# Revit family: Bath-Freestanding-KOHLER-ARCHER-K-45594T_1
name_source: partatom
category: Plumbing Fixtures
revit_build: Autodesk Revit 2017 (Build: 20160225_1515(x64)
units: mm (PartAtom-declared; Revit-internal decimal feet)

## family parameters
Cut with Voids When Loaded = No
Host = Face
OmniClass Number = 23.31.15.00
OmniClass Title = Bathtubs
Part Type = Normal
Room Calculation Point = No
Round Connector Dimension = Use Diameter
Shared = No

## types (2) — shared parameters
ADA Compliant = No
Assembly Code = D2010500
CW Connection = No
Cold Water Inlet = Cold Water Inlet
Date Modified = 04/13/2020
Default Elevation = 0"
Description = ARCHER 1.5M CAST IRON FREESTANDING BATH
Drain Included = Yes
Finish = KOHLER-Cast_Iron-0-White
HW Connection = No
Height = 21 7/16"
Hot Water Inlet = Hot Water Inlet
Length = 59 1/16"
Manufacturer = KOHLER Co.
Master Format 2014 = 22 41 19
Master Format 2014 Name = Residential Bathtubs
Material = Cast Iron
Product Documentation Link = http://files.kohler.com.cn
Product Name = ARCHER
Product Page URL = http://www.kohler.com.cn
URL = http://www.kohler.com.cn
Vent Connection = No
Waste Connection = Yes
Waste Water Outlet = Waste Water Outlet
WaterSense Certified = No
Width = 29 1/2"

## per-type parameters (varying)
| type | Armrest | Model | Type | Without Armrest |
| Without Armrest, 0-White | No | K-45594T-0 | 1 | Yes |
| With Armrest, 0-White | Yes | K-45594T-GR-0 | 2 | No |

## geometry (parser evidence)
native form markers: Sweep x6
no freeform markers — native parametric forms only
